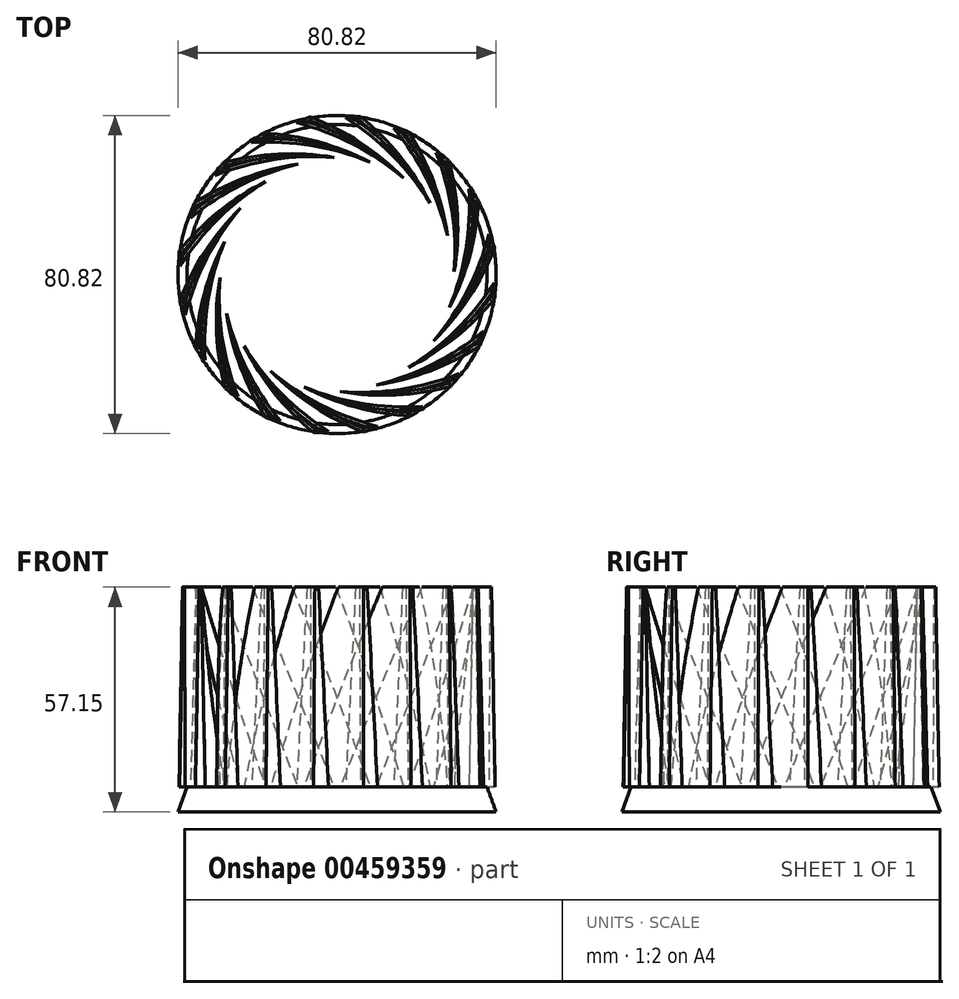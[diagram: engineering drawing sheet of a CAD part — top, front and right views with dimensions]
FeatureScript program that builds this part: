
annotation { "Feature Type Name" : "Feature", "Feature Type Description" : "" }
export const myFeature = defineFeature(function(context is Context, id is Id, definition is map)
    precondition{}
    {
        {
            var Q0;
            Q0=qCreatedBy(makeId("Top.planeOp"),FACE);
            var sketch = newSketch(context, id + "F0", { "sketchPlane" : qUnion([Q0])});
            skCircle(sketch, "E0", {"center": v(0, 0) * mm, "radius": 38.1 * mm, "construction": true});
            skArc(sketch, "E1.trimOffspring", {"start": v(28.05, 9.97) * mm, "mid": v(24.47, 23.69) * mm, "end": v(18.07, 36.35) * mm});
            skArc(sketch, "E2.trimOffspring", {"start": v(28.05, 9.97) * mm, "mid": v(22.77, 24.38) * mm, "end": v(14.36, 37.23) * mm});
            skArc(sketch, "E3.trimOffspring", {"start": v(18.07, 36.35) * mm, "mid": v(16.23, 36.85) * mm, "end": v(14.36, 37.23) * mm});
            skArc(sketch, "E4.1.0", {"start": v(5.95, 40.15) * mm, "mid": v(4.05, 40.06) * mm, "end": v(2.16, 39.85) * mm});
            skArc(sketch, "E4.1.1", {"start": v(23.6, 18.15) * mm, "mid": v(15.95, 30.1) * mm, "end": v(5.95, 40.15) * mm});
            skArc(sketch, "E4.1.2", {"start": v(23.6, 18.15) * mm, "mid": v(14.12, 30.22) * mm, "end": v(2.16, 39.85) * mm});
            skArc(sketch, "E4.2.0", {"start": v(-6.75, 40.02) * mm, "mid": v(-8.53, 39.35) * mm, "end": v(-10.26, 38.56) * mm});
            skArc(sketch, "E4.2.1", {"start": v(16.84, 24.55) * mm, "mid": v(5.87, 33.55) * mm, "end": v(-6.75, 40.02) * mm});
            skArc(sketch, "E4.2.2", {"start": v(16.84, 24.55) * mm, "mid": v(4.09, 33.1) * mm, "end": v(-10.26, 38.56) * mm});
            skArc(sketch, "E5.1.3.0", {"start": v(-18.78, 35.98) * mm, "mid": v(-20.27, 34.8) * mm, "end": v(-21.68, 33.5) * mm});
            skArc(sketch, "E5.4.3.0", {"start": v(8.43, 28.56) * mm, "mid": v(-4.78, 33.72) * mm, "end": v(-18.78, 35.98) * mm});
            skArc(sketch, "E5.8.3.0", {"start": v(8.43, 28.56) * mm, "mid": v(-6.34, 32.75) * mm, "end": v(-21.68, 33.5) * mm});
            skArc(sketch, "E5.1.4.0", {"start": v(-28.98, 28.41) * mm, "mid": v(-30.03, 26.82) * mm, "end": v(-30.97, 25.17) * mm});
            skArc(sketch, "E5.4.4.0", {"start": v(-0.8, 29.76) * mm, "mid": v(-14.97, 30.59) * mm, "end": v(-28.98, 28.41) * mm});
            skArc(sketch, "E5.8.4.0", {"start": v(-0.8, 29.76) * mm, "mid": v(-16.15, 29.19) * mm, "end": v(-30.97, 25.17) * mm});
            skArc(sketch, "E5.1.5.0", {"start": v(-36.35, 18.07) * mm, "mid": v(-36.85, 16.23) * mm, "end": v(-37.23, 14.36) * mm});
            skArc(sketch, "E5.4.5.0", {"start": v(-9.97, 28.05) * mm, "mid": v(-23.69, 24.47) * mm, "end": v(-36.35, 18.07) * mm});
            skArc(sketch, "E5.8.5.0", {"start": v(-9.97, 28.05) * mm, "mid": v(-24.38, 22.77) * mm, "end": v(-37.23, 14.36) * mm});
            skArc(sketch, "E5.1.6.0", {"start": v(-40.15, 5.95) * mm, "mid": v(-40.06, 4.05) * mm, "end": v(-39.85, 2.16) * mm});
            skArc(sketch, "E5.4.6.0", {"start": v(-18.15, 23.6) * mm, "mid": v(-30.1, 15.95) * mm, "end": v(-40.15, 5.95) * mm});
            skArc(sketch, "E5.8.6.0", {"start": v(-18.15, 23.6) * mm, "mid": v(-30.22, 14.12) * mm, "end": v(-39.85, 2.16) * mm});
            skArc(sketch, "E5.1.7.0", {"start": v(-40.02, -6.75) * mm, "mid": v(-39.35, -8.53) * mm, "end": v(-38.56, -10.26) * mm});
            skArc(sketch, "E5.4.7.0", {"start": v(-24.55, 16.84) * mm, "mid": v(-33.55, 5.87) * mm, "end": v(-40.02, -6.75) * mm});
            skArc(sketch, "E5.8.7.0", {"start": v(-24.55, 16.84) * mm, "mid": v(-33.1, 4.09) * mm, "end": v(-38.56, -10.26) * mm});
            skArc(sketch, "E5.1.8.0", {"start": v(-35.98, -18.78) * mm, "mid": v(-34.8, -20.27) * mm, "end": v(-33.5, -21.68) * mm});
            skArc(sketch, "E5.4.8.0", {"start": v(-28.56, 8.43) * mm, "mid": v(-33.72, -4.78) * mm, "end": v(-35.98, -18.78) * mm});
            skArc(sketch, "E5.8.8.0", {"start": v(-28.56, 8.43) * mm, "mid": v(-32.75, -6.34) * mm, "end": v(-33.5, -21.68) * mm});
            skArc(sketch, "E5.1.9.0", {"start": v(-28.41, -28.98) * mm, "mid": v(-26.82, -30.03) * mm, "end": v(-25.17, -30.97) * mm});
            skArc(sketch, "E5.4.9.0", {"start": v(-29.76, -0.8) * mm, "mid": v(-30.59, -14.97) * mm, "end": v(-28.41, -28.98) * mm});
            skArc(sketch, "E5.8.9.0", {"start": v(-29.76, -0.8) * mm, "mid": v(-29.19, -16.15) * mm, "end": v(-25.17, -30.97) * mm});
            skArc(sketch, "E5.1.10.0", {"start": v(-18.07, -36.35) * mm, "mid": v(-16.23, -36.85) * mm, "end": v(-14.36, -37.23) * mm});
            skArc(sketch, "E5.4.10.0", {"start": v(-28.05, -9.97) * mm, "mid": v(-24.47, -23.69) * mm, "end": v(-18.07, -36.35) * mm});
            skArc(sketch, "E5.8.10.0", {"start": v(-28.05, -9.97) * mm, "mid": v(-22.77, -24.38) * mm, "end": v(-14.36, -37.23) * mm});
            skArc(sketch, "E5.1.11.0", {"start": v(-5.95, -40.15) * mm, "mid": v(-4.05, -40.06) * mm, "end": v(-2.16, -39.85) * mm});
            skArc(sketch, "E5.4.11.0", {"start": v(-23.6, -18.15) * mm, "mid": v(-15.95, -30.1) * mm, "end": v(-5.95, -40.15) * mm});
            skArc(sketch, "E5.8.11.0", {"start": v(-23.6, -18.15) * mm, "mid": v(-14.12, -30.22) * mm, "end": v(-2.16, -39.85) * mm});
            skArc(sketch, "E5.1.12.0", {"start": v(6.75, -40.02) * mm, "mid": v(8.53, -39.35) * mm, "end": v(10.26, -38.56) * mm});
            skArc(sketch, "E5.4.12.0", {"start": v(-16.84, -24.55) * mm, "mid": v(-5.87, -33.55) * mm, "end": v(6.75, -40.02) * mm});
            skArc(sketch, "E5.8.12.0", {"start": v(-16.84, -24.55) * mm, "mid": v(-4.09, -33.1) * mm, "end": v(10.26, -38.56) * mm});
            skArc(sketch, "E5.1.13.0", {"start": v(18.78, -35.98) * mm, "mid": v(20.27, -34.8) * mm, "end": v(21.68, -33.5) * mm});
            skArc(sketch, "E5.4.13.0", {"start": v(-8.43, -28.56) * mm, "mid": v(4.78, -33.72) * mm, "end": v(18.78, -35.98) * mm});
            skArc(sketch, "E5.8.13.0", {"start": v(-8.43, -28.56) * mm, "mid": v(6.34, -32.75) * mm, "end": v(21.68, -33.5) * mm});
            skArc(sketch, "E5.1.14.0", {"start": v(28.98, -28.41) * mm, "mid": v(30.03, -26.82) * mm, "end": v(30.97, -25.17) * mm});
            skArc(sketch, "E5.4.14.0", {"start": v(0.8, -29.76) * mm, "mid": v(14.97, -30.59) * mm, "end": v(28.98, -28.41) * mm});
            skArc(sketch, "E5.8.14.0", {"start": v(0.8, -29.76) * mm, "mid": v(16.15, -29.19) * mm, "end": v(30.97, -25.17) * mm});
            skArc(sketch, "E5.1.15.0", {"start": v(36.35, -18.07) * mm, "mid": v(36.85, -16.23) * mm, "end": v(37.23, -14.36) * mm});
            skArc(sketch, "E5.4.15.0", {"start": v(9.97, -28.05) * mm, "mid": v(23.69, -24.47) * mm, "end": v(36.35, -18.07) * mm});
            skArc(sketch, "E5.8.15.0", {"start": v(9.97, -28.05) * mm, "mid": v(24.38, -22.77) * mm, "end": v(37.23, -14.36) * mm});
            skArc(sketch, "E5.1.16.0", {"start": v(40.15, -5.95) * mm, "mid": v(40.06, -4.05) * mm, "end": v(39.85, -2.16) * mm});
            skArc(sketch, "E5.4.16.0", {"start": v(18.15, -23.6) * mm, "mid": v(30.1, -15.95) * mm, "end": v(40.15, -5.95) * mm});
            skArc(sketch, "E5.8.16.0", {"start": v(18.15, -23.6) * mm, "mid": v(30.22, -14.12) * mm, "end": v(39.85, -2.16) * mm});
            skArc(sketch, "E5.1.17.0", {"start": v(40.02, 6.75) * mm, "mid": v(39.35, 8.53) * mm, "end": v(38.56, 10.26) * mm});
            skArc(sketch, "E5.4.17.0", {"start": v(24.55, -16.84) * mm, "mid": v(33.55, -5.87) * mm, "end": v(40.02, 6.75) * mm});
            skArc(sketch, "E5.8.17.0", {"start": v(24.55, -16.84) * mm, "mid": v(33.1, -4.09) * mm, "end": v(38.56, 10.26) * mm});
            skArc(sketch, "E5.1.18.0", {"start": v(35.98, 18.78) * mm, "mid": v(34.8, 20.27) * mm, "end": v(33.5, 21.68) * mm});
            skArc(sketch, "E5.4.18.0", {"start": v(28.56, -8.43) * mm, "mid": v(33.72, 4.78) * mm, "end": v(35.98, 18.78) * mm});
            skArc(sketch, "E5.8.18.0", {"start": v(28.56, -8.43) * mm, "mid": v(32.75, 6.34) * mm, "end": v(33.5, 21.68) * mm});
            skArc(sketch, "E5.1.19.0", {"start": v(28.41, 28.98) * mm, "mid": v(26.82, 30.03) * mm, "end": v(25.17, 30.97) * mm});
            skArc(sketch, "E5.4.19.0", {"start": v(29.76, 0.8) * mm, "mid": v(30.59, 14.97) * mm, "end": v(28.41, 28.98) * mm});
            skArc(sketch, "E5.8.19.0", {"start": v(29.76, 0.8) * mm, "mid": v(29.19, 16.15) * mm, "end": v(25.17, 30.97) * mm});
            skSolve(sketch);
        }
        {
            var Q0;
            Q0 = qSketchRegion(id + "F0", true);
            extrude(context, id + "F1", {"entities" : qUnion([Q0]), "depth" : 50.8 * mm, "hasDraft" : true, "draftAngle" : 1 * degree, "draftPullDirection" : true});
        }
        {
            var Q0;
            Q0=qCreatedBy(makeId("Top.planeOp"),FACE);
            var sketch = newSketch(context, id + "F2", { "sketchPlane" : qUnion([Q0])});
            skCircle(sketch, "E6", {"center": v(0, 0) * mm, "radius": 38.1 * mm});
            skSolve(sketch);
        }
        {
            var Q0;
            Q0 = qSketchRegion(id + "F2", true);
            extrude(context, id + "F3", {"entities" : qUnion([Q0]), "oppositeDirection" : true, "depth" : 6.35 * mm, "hasDraft" : true, "draftAngle" : 20 * degree});
        }
    });
